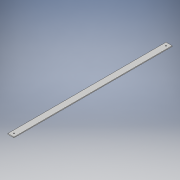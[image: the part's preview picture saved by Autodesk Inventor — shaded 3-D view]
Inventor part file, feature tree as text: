
AUTODESK INVENTOR PART (.ipt)
format: ipt  version: 2018 (Build 220112000, 112)  size: 106,496 bytes
history: native  units: in
note: dims shown in document units (in); Inventor stores cm internally (conversion verified against a paired STEP export)
features: extrude x2, sketch x2
ambient origin geometry x8: Origin, YZ Plane, XZ Plane, XY Plane, X Axis, Y Axis, Z Axis, Center Point
bodies: Solid1 (feature_tree)
feature tree (4):
  extrude  "Extrusion1"  Depth=1.0in
  extrude  "Extrusion6"  Depth=0.125in
  sketch  "Sketch1"  dims[d5=26.0in d6=0.0in d23=1.0in]
  sketch  "Sketch6"  dims[d24=0.125in d25=0.5in d26=0.5in d27=0.2031in d28=24.0in d29=0.0in]
